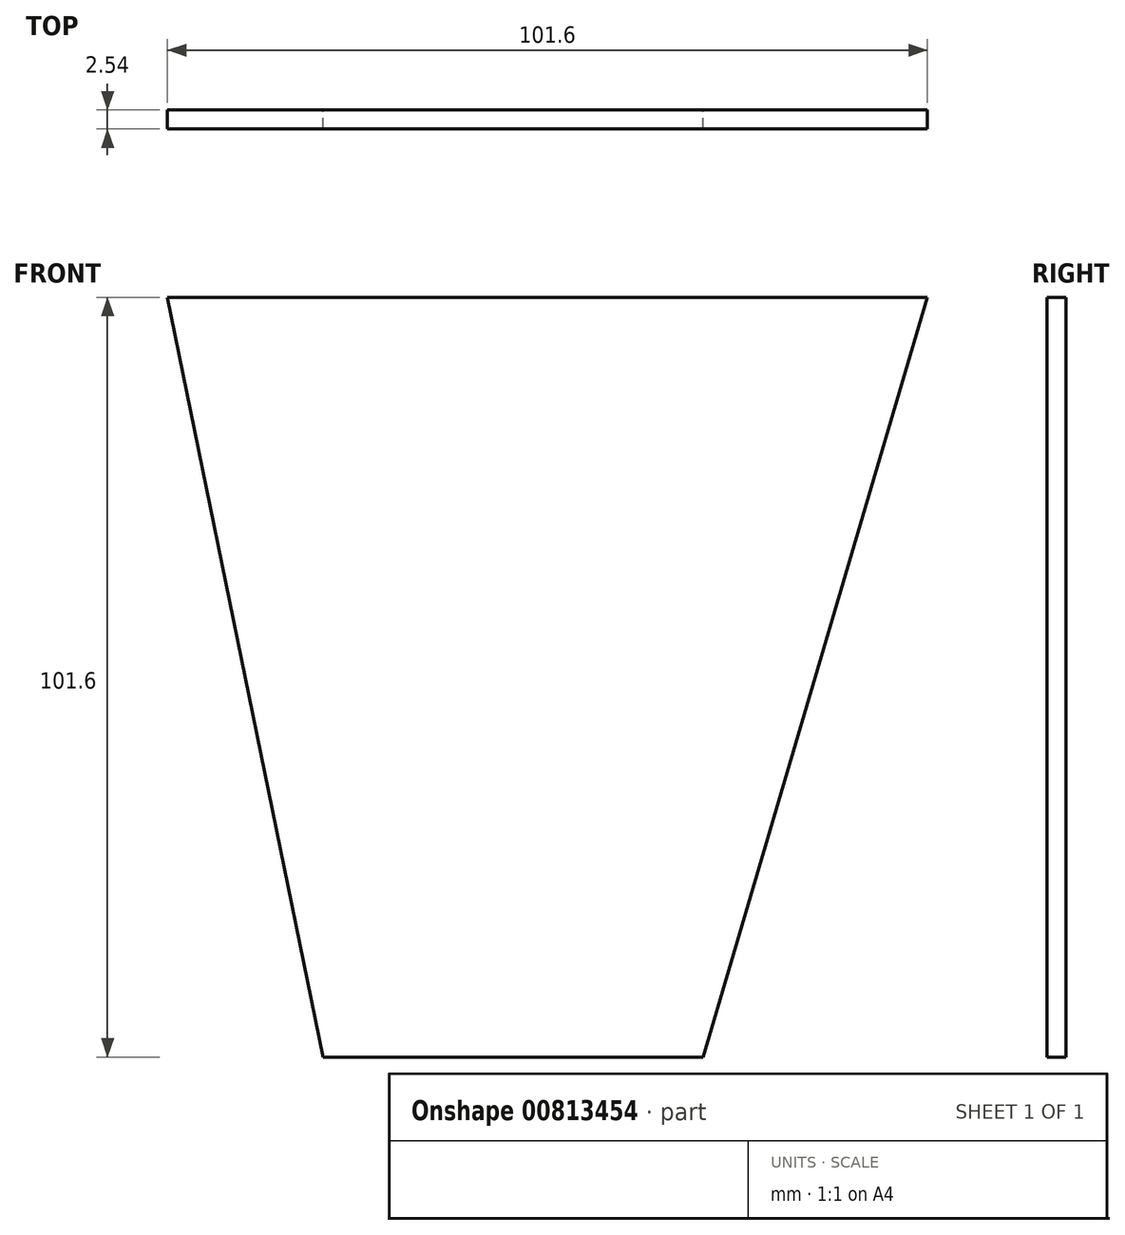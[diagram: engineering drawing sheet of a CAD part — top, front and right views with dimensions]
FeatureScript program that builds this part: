
annotation { "Feature Type Name" : "Feature", "Feature Type Description" : "" }
export const myFeature = defineFeature(function(context is Context, id is Id, definition is map)
    precondition{}
    {
        {
            var Q0;
            Q0=qCreatedBy(makeId("Front.planeOp"),FACE);
            var sketch = newSketch(context, id + "F0", { "sketchPlane" : qUnion([Q0])});
            skLineSegment(sketch, "E0", {"start": v(-50.31, 37.12) * mm, "end": v(51.29, 37.12) * mm});
            skLineSegment(sketch, "E1", {"start": v(51.29, 37.12) * mm, "end": v(21.33, -64.48) * mm});
            skLineSegment(sketch, "E2", {"start": v(21.33, -64.48) * mm, "end": v(-29.47, -64.48) * mm});
            skLineSegment(sketch, "E3", {"start": v(-29.47, -64.48) * mm, "end": v(-50.31, 37.12) * mm});
            skLineSegment(sketch, "E4", {"start": v(-29.47, -64.48) * mm, "end": v(-29.47, 37.12) * mm});
            skSolve(sketch);
        }
        {
            var Q0;
            {var subQ0=sQuery(id+"F0.wireOp",EDGE,"E1");Q0=makeQuery(id+"F0.imprint","IMPRINT",FACE,{"disambiguationData":[TD([[makeQuery(id+"F0.imprint","IMPRINT",EDGE,{"derivedFrom":subQ0}),-1.0]])]});}
            var Q1;
            {var subQ0=sQuery(id+"F0.wireOp",EDGE,"E3");Q1=makeQuery(id+"F0.imprint","IMPRINT",FACE,{"disambiguationData":[TD([[makeQuery(id+"F0.imprint","IMPRINT",EDGE,{"derivedFrom":subQ0}),-1.0]])]});}
            extrude(context, id + "F1", {"entities" : qUnion([Q0, Q1]), "depth" : 2.54 * mm, "offsetDistance" : 25.4 * mm});
        }
    });
